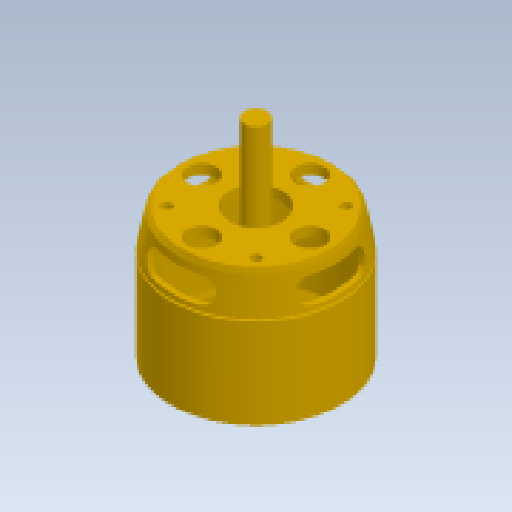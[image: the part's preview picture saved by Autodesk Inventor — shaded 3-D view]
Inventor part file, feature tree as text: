
AUTODESK INVENTOR PART (.ipt)
format: ipt  version: 2023 (Build 270158000, 158)  size: 349,184 bytes
history: native  units: in
note: dims shown in document units (in); Inventor stores cm internally (conversion verified against a paired STEP export)
features: extrude x4, sketch x4, pattern_circular x2, revolve x1, plane x1
ambient origin geometry x8: Origin, YZ Plane, XZ Plane, XY Plane, X Axis, Y Axis, Z Axis, Center Point
bodies: Solid1 (feature_tree)
feature tree (12):
  revolve  "Revolution1"  [1 undecoded]
  extrude  "Extrusion1"  Depth=0.5161in
  plane  "Work Plane1"
  extrude  "Extrusion2"  Depth=0.0787in
  sketch  "Sketch4"  dims[d6=45.0deg d7=0.3616in d8=0.0315in d9=1.2252in d10=0.1102in d11=0.1575in d12=3.2677in d13=1.0433in d14=0.0835in d16=0.0709in d17=0.1102in d18=0.3248in d19=0.6713in d20=90.0deg d21=0.3878in d22=0.128in d23=45.0deg d24=0.8661in d25=0.7382in d26=0.3937in d27=0.0in d28=1.1875in d29=0.315in d30=0.315in d31=0.2165in d32=0.6299in d33=0.3937in d34=0.0in d35=0.0906in d36=0.3937in d37=45.0deg d38=0.3937in d39=0.0in d40=1.5748in d41=360.0deg d43=0.9843in d44=2.0472in d46=0.3937in d47=0.0787in d48=0.3937in d49=0.0in d50=1.9685in d51=360.0deg]
  extrude  "Extrusion3"  Depth=0.3937in
  pattern_circular  "Circular Pattern1"  [2 undecoded]
  extrude  "Extrusion4"  Depth=0.3937in
  pattern_circular  "Circular Pattern2"  [2 undecoded]
  sketch  "Sketch1"  dims[d0=0.1378in d1=1.1614in]
  sketch  "Sketch2"  dims[d2=0.0709in d3=0.5161in]
  sketch  "Sketch3"  dims[d4=1.0573in d5=0.0787in]
note: 5 required parameter values undecoded (feature->parameter linkage not recoverable at this tier; creation-order binding heuristic only, values carry confidence <= 0.55)